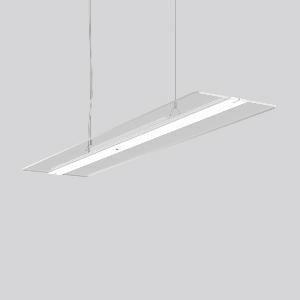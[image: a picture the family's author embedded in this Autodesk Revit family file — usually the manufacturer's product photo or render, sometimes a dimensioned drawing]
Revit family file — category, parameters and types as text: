
# Revit family: twindot_k_312264_002_1_19_39e7
name_source: partatom
category: Lighting Fixtures
units: mm (PartAtom-declared; Revit-internal decimal feet)

## family parameters
Cut with Voids When Loaded = No
Host = Face
Light Source = No
Part Type = Normal
Room Calculation Point = No
Round Connector Dimension = Use Diameter
Shared = No

## types (1)
- TWINDOT K (1 x LED Modul 840, 8100 lm, 4000)
    Apparent Load = 62 VA
    CIE Flux Codes = 47 77 94 55 100
    Color Rendering = 80
    Color Temperature = 4000
    Default Elevation = 1800 mm
    Description = Series: TWINDOT K
LED pendant luminaire with extremely flat and frameless appearance. Middle bar made of aluminium extrusion profile, powder-coated. Transparent light guide made of UV-resistant acrylic glass (PMMA) with TWINDOT prismatic. Light control with perfectly glare-free TWINDOT technology for pleasantly gentle light with soft shadows. Even and wide indirect and direct light distribution. Direct 55%, indirect 45% light emission. 2 point steel cable suspension, height adjustable steplessly with transparent power cable. Converter integrated in the middle bar. Integrated sensor for daylight and occupancy-dependent light control. Presence detection range adjustable via integrated shutters between 40° and 90°. Light sensor range: 20-800 lx (measured at the sensor). Installation height: 2-5 m. Detection range (at a height of 2.5 m): Ø 1.8-5 m. Max. detection range (at the maximum mounting height of 5 m): Ø 7 m. Perfect for office areas (RUG < 19) and environments with computer screens in accordance with EN 12464-1. 
Colour: traffic white, matt (RAL 9016)
Length: 1500 mm
Width: 350 mm
Height: 45 mm
Suspension length: 500-1200 mm
Lamp: LED
Socket: without socket
Colour temperature: 4000K
Colour rendering index (CRI): 80
System power: 62 W
Rated luminous flux: 8100 lm
Beam angle Down: 91° / 102°
Luminous efficiency: 131 lm/W
Control gear: Sensor converter
Protection class: I
Type of protection: IP 20
    Height = 45 mm
    Lamp = 1 x LED Modul 840
    Lamp Light Flux = 8100 lm
    Lamp count = 1
    Length = 1500 mm
    Lifetime = 50000 h
    Luminous efficacy = 131 lm/W
    Manufacturer = RZB
    ModVariant = No
    Model = 312264.002.1.19
    Mounting Place = Ceiling
    Mounting Type = Pendant
    Number of Poles = 1
    OnlyDefault = Yes
    Power Factor = 1
    Product Name = TWINDOT K
    Product group = Pendant modular luminaires
    ProductGroupID = 906
    Protection Class = Protection class I
    Protection Degree = IP 20
    RLX_Detail_Level = 1
    RLX_Emergency_Light_Flux = 0 lm
    RLX_Emergency_Type = 0
    RLX_Emergency_Type_DB = No
    RlxData = <blob elided: 35521 chars, md5=230146e3>
    Socket = socket
    Standby Power = 0 W
    System Light Flux = 8100 lm
    System Power = 62 W
    Type Comments = ALEA SPOT
    Type Image = 312264.002.19.jpg
    URL = http://relux.com
    VarID = ---
    Voltage = 230 V
    Voltage Range = 220-240 V
    Weight = 0.00 kg
    Width = 350 mm

## geometry (parser evidence)
native form markers: Blend x4, Sweep x12
no freeform markers — native parametric forms only
